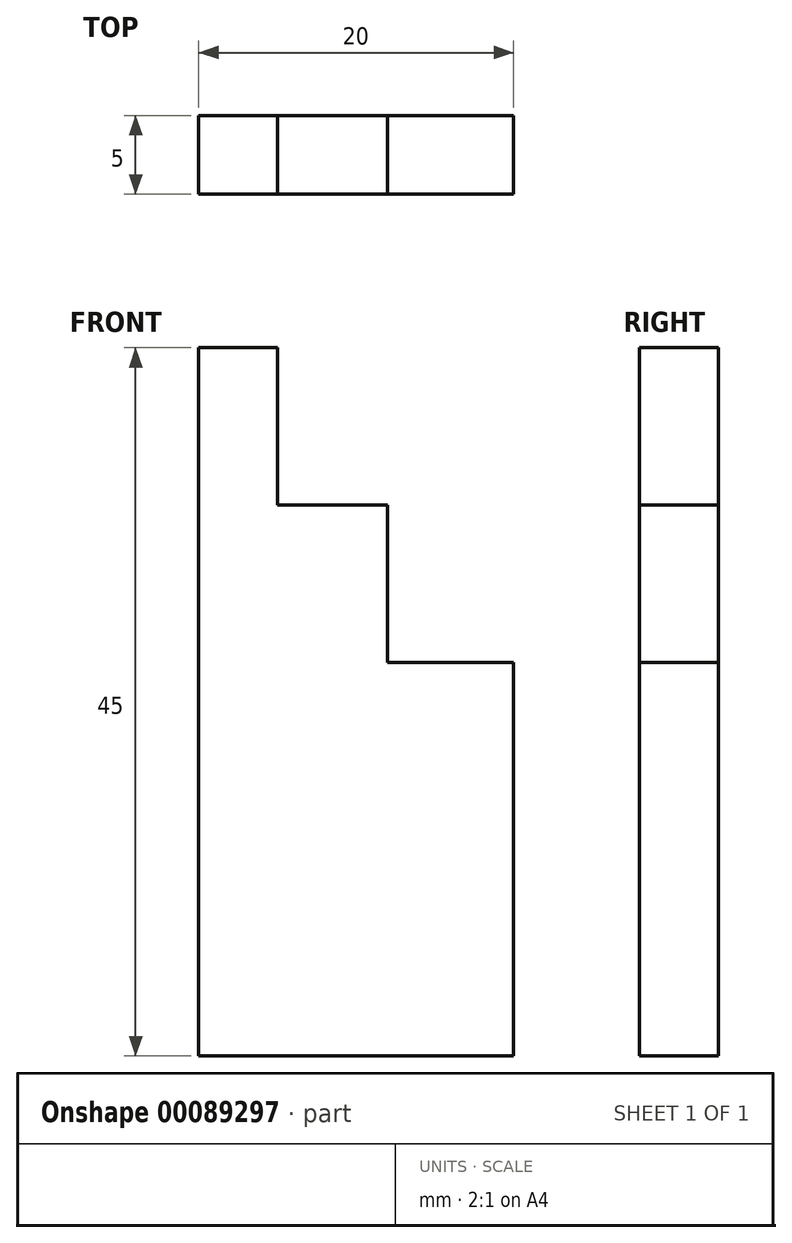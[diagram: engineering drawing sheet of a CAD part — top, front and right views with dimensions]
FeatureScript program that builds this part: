
annotation { "Feature Type Name" : "Feature", "Feature Type Description" : "" }
export const myFeature = defineFeature(function(context is Context, id is Id, definition is map)
    precondition{}
    {
        {
            var Q0;
            Q0=qCreatedBy(makeId("Front.planeOp"),FACE);
            var sketch = newSketch(context, id + "F0", { "sketchPlane" : qUnion([Q0])});
            skLineSegment(sketch, "E0.bottom", {"start": v(-10, 22.5) * mm, "end": v(-5, 22.5) * mm});
            skLineSegment(sketch, "E0.top", {"start": v(-10, -22.5) * mm, "end": v(10, -22.5) * mm});
            skLineSegment(sketch, "E0.left", {"start": v(-10, 22.5) * mm, "end": v(-10, -22.5) * mm});
            skLineSegment(sketch, "E0.right", {"start": v(10, 2.5) * mm, "end": v(10, -22.5) * mm});
            skPoint(sketch, "E0.middle", {"position": v(0, 0) * mm});
            skLineSegment(sketch, "E1", {"start": v(-5, 22.5) * mm, "end": v(-5, 12.5) * mm});
            skLineSegment(sketch, "E2", {"start": v(-5, 12.5) * mm, "end": v(2, 12.5) * mm});
            skLineSegment(sketch, "E3", {"start": v(2, 12.5) * mm, "end": v(2, 2.5) * mm});
            skLineSegment(sketch, "E4", {"start": v(2, 2.5) * mm, "end": v(10, 2.5) * mm});
            skSolve(sketch);
        }
        {
            var Q0;
            Q0 = qSketchRegion(id + "F0", true);
            extrude(context, id + "F1", {"entities" : qUnion([Q0]), "depth" : 5 * mm});
        }
    });
